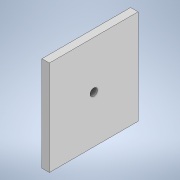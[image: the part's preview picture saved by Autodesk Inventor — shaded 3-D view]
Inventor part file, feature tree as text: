
AUTODESK INVENTOR PART (.ipt)
format: ipt  version: 2022 (Build 260153000, 153)  size: 107,008 bytes
history: native  units: mm
features: extrude x3, sketch x3
ambient origin geometry x8: Origin, YZ Plane, XZ Plane, XY Plane, X Axis, Y Axis, Z Axis, Center Point
bodies: Solid1 (feature_tree)
feature tree (6):
  extrude  "Extrusion1"  Depth=94.996mm
  extrude  "Extrusion2"  Depth=4.0mm
  extrude  "Extrusion3"  Depth=8.0mm
  sketch  "Sketch1"  dims[d0=101.6mm d1=94.996mm]
  sketch  "Sketch2"  dims[d2=8.0mm d3=0.0mm d6=4.0mm]
  sketch  "Sketch3"  dims[d7=8.0mm d8=0.0mm d9=8.0mm d10=0.0mm d11=0.0mm]
